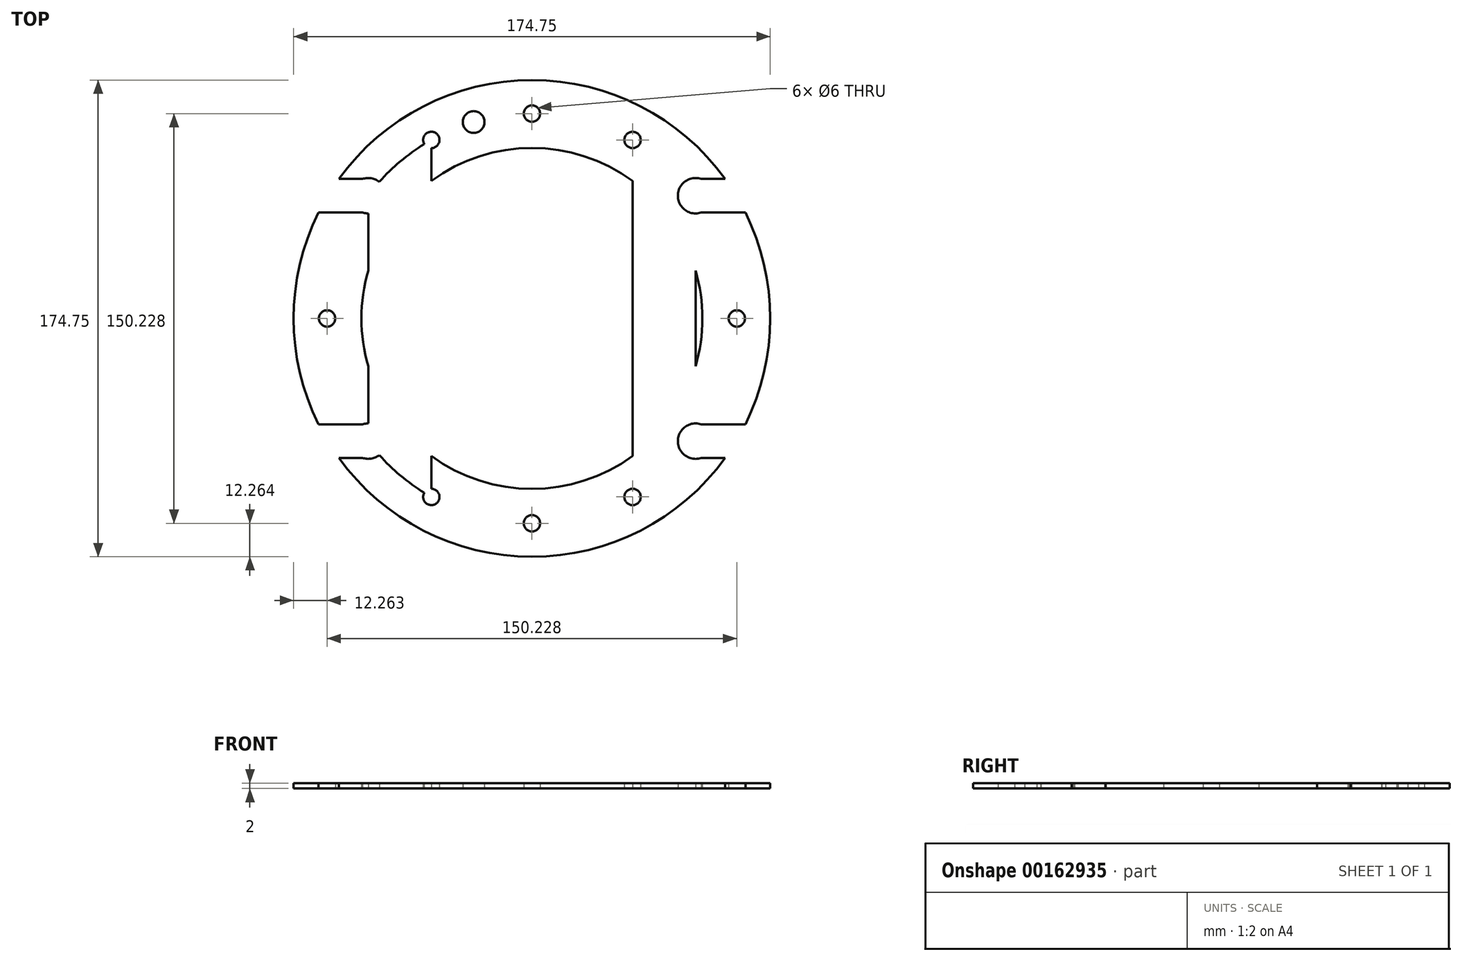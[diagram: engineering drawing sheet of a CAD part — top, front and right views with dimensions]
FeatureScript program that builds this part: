
annotation { "Feature Type Name" : "Feature", "Feature Type Description" : "" }
export const myFeature = defineFeature(function(context is Context, id is Id, definition is map)
    precondition{}
    {
        {
            var Q0;
            Q0=qCreatedBy(makeId("Top.planeOp"),FACE);
            var sketch = newSketch(context, id + "F0", { "sketchPlane" : qUnion([Q0])});
            skLineSegment(sketch, "E0.bottom", {"start": v(60.27, 43.84) * mm, "end": v(-59.73, 43.84) * mm});
            skLineSegment(sketch, "E0.top", {"start": v(60.27, -46.16) * mm, "end": v(-59.73, -46.16) * mm});
            skLineSegment(sketch, "E0.left", {"start": v(60.27, 43.84) * mm, "end": v(60.27, -46.16) * mm});
            skLineSegment(sketch, "E0.right", {"start": v(-59.73, 43.84) * mm, "end": v(-59.73, -46.16) * mm});
            skPoint(sketch, "E0.middle", {"position": v(0.27, -1.16) * mm});
            skCircle(sketch, "E1", {"center": v(60.27, 43.84) * mm, "radius": 6.5 * mm});
            skCircle(sketch, "E2", {"center": v(-59.73, 43.84) * mm, "radius": 6.5 * mm});
            skCircle(sketch, "E3", {"center": v(60.27, -46.16) * mm, "radius": 6.5 * mm});
            skCircle(sketch, "E4", {"center": v(-59.73, -46.16) * mm, "radius": 6.5 * mm});
            skCircle(sketch, "E5", {"center": v(0.27, -1.16) * mm, "radius": 87.38 * mm});
            skLineSegment(sketch, "E6.bottom", {"start": v(58.16, 49.99) * mm, "end": v(62.37, 49.99) * mm});
            skLineSegment(sketch, "E6.top", {"start": v(58.16, 37.69) * mm, "end": v(62.37, 37.69) * mm});
            skLineSegment(sketch, "E6.left", {"start": v(58.16, 49.99) * mm, "end": v(58.16, 37.69) * mm});
            skLineSegment(sketch, "E6.right", {"start": v(62.37, 49.99) * mm, "end": v(62.37, 37.69) * mm});
            skLineSegment(sketch, "E7.bottom", {"start": v(-61.84, 49.99) * mm, "end": v(-57.63, 49.99) * mm});
            skLineSegment(sketch, "E7.top", {"start": v(-61.84, 37.69) * mm, "end": v(-57.63, 37.69) * mm});
            skLineSegment(sketch, "E7.left", {"start": v(-61.84, 49.99) * mm, "end": v(-61.84, 37.69) * mm});
            skLineSegment(sketch, "E7.right", {"start": v(-57.63, 49.99) * mm, "end": v(-57.63, 37.69) * mm});
            skLineSegment(sketch, "E8.bottom", {"start": v(62.37, -40.01) * mm, "end": v(58.16, -40.01) * mm});
            skLineSegment(sketch, "E8.top", {"start": v(62.37, -52.31) * mm, "end": v(58.16, -52.31) * mm});
            skLineSegment(sketch, "E8.left", {"start": v(62.37, -40.01) * mm, "end": v(62.37, -52.31) * mm});
            skLineSegment(sketch, "E8.right", {"start": v(58.16, -40.01) * mm, "end": v(58.16, -52.31) * mm});
            skLineSegment(sketch, "E9.bottom", {"start": v(-61.84, -40.01) * mm, "end": v(-57.63, -40.01) * mm});
            skLineSegment(sketch, "E9.top", {"start": v(-61.84, -52.31) * mm, "end": v(-57.63, -52.31) * mm});
            skLineSegment(sketch, "E9.left", {"start": v(-61.84, -40.01) * mm, "end": v(-61.84, -52.31) * mm});
            skLineSegment(sketch, "E9.right", {"start": v(-57.63, -40.01) * mm, "end": v(-57.63, -52.31) * mm});
            skLineSegment(sketch, "E10.bottom", {"start": v(58.16, -40.01) * mm, "end": v(80.94, -40.01) * mm});
            skLineSegment(sketch, "E10.top", {"start": v(58.16, -52.31) * mm, "end": v(80.94, -52.31) * mm});
            skLineSegment(sketch, "E10.right", {"start": v(80.94, -40.01) * mm, "end": v(80.94, -52.31) * mm});
            skLineSegment(sketch, "E11.bottom", {"start": v(58.16, 49.99) * mm, "end": v(78.53, 49.99) * mm});
            skLineSegment(sketch, "E11.top", {"start": v(58.16, 37.69) * mm, "end": v(78.53, 37.69) * mm});
            skLineSegment(sketch, "E11.right", {"start": v(78.53, 49.99) * mm, "end": v(78.53, 37.69) * mm});
            skLineSegment(sketch, "E12.bottom", {"start": v(-57.63, 49.99) * mm, "end": v(-78, 49.99) * mm});
            skLineSegment(sketch, "E12.top", {"start": v(-57.63, 37.69) * mm, "end": v(-78, 37.69) * mm});
            skLineSegment(sketch, "E12.right", {"start": v(-78, 49.99) * mm, "end": v(-78, 37.69) * mm});
            skLineSegment(sketch, "E13.bottom", {"start": v(-57.63, -40.01) * mm, "end": v(-78, -40.01) * mm});
            skLineSegment(sketch, "E13.top", {"start": v(-57.63, -52.31) * mm, "end": v(-78, -52.31) * mm});
            skLineSegment(sketch, "E13.right", {"start": v(-78, -40.01) * mm, "end": v(-78, -52.31) * mm});
            skCircle(sketch, "E14", {"center": v(0.27, -1.16) * mm, "radius": 62.5 * mm});
            skCircle(sketch, "E15", {"center": v(0.27, 73.95) * mm, "radius": 3 * mm});
            skCircle(sketch, "E16", {"center": v(0.27, -76.28) * mm, "radius": 3 * mm});
            skCircle(sketch, "E17", {"center": v(75.38, -1.16) * mm, "radius": 3 * mm});
            skCircle(sketch, "E18", {"center": v(-74.85, -1.16) * mm, "radius": 3 * mm});
            skCircle(sketch, "E19", {"center": v(-21.11, 70.87) * mm, "radius": 4 * mm});
            skCircle(sketch, "E20", {"center": v(0.27, -1.16) * mm, "radius": 75.13 * mm});
            skLineSegment(sketch, "E21.bottom", {"start": v(37.16, 64.3) * mm, "end": v(-36.63, 64.3) * mm});
            skLineSegment(sketch, "E21.top", {"start": v(37.16, -66.61) * mm, "end": v(-36.63, -66.61) * mm});
            skLineSegment(sketch, "E21.left", {"start": v(37.16, 64.3) * mm, "end": v(37.16, -66.61) * mm});
            skLineSegment(sketch, "E21.right", {"start": v(-36.63, 64.3) * mm, "end": v(-36.63, -66.61) * mm});
            skCircle(sketch, "E22", {"center": v(-36.63, 64.3) * mm, "radius": 3 * mm});
            skCircle(sketch, "E23", {"center": v(37.16, 64.3) * mm, "radius": 3 * mm});
            skCircle(sketch, "E24", {"center": v(37.16, -66.61) * mm, "radius": 3 * mm});
            skCircle(sketch, "E25", {"center": v(-36.63, -66.61) * mm, "radius": 3 * mm});
            skSolve(sketch);
        }
        {
            var Q0;
            {var subQ0=sQuery(id+"F0.wireOp",EDGE,"E11.bottom");var subQ3=sQuery(id+"F0.wireOp",EDGE,"E5");var subQ4=makeQuery(id+"F0.imprint","INTERSECT",VERTEX,{"derivedFrom":[subQ3,subQ0]});Q0=makeQuery(id+"F0.imprint","IMPRINT",FACE,{"disambiguationData":[TD([[makeQuery(id+"F0.imprint","IMPRINT",EDGE,{"disambiguationData":[TD([[subQ4,-1.0]])],"derivedFrom":subQ3}),1.0]])]});}
            var Q1;
            {var subQ0=sQuery(id+"F0.wireOp",EDGE,"E20");var subQ1=sQuery(id+"F0.wireOp",EDGE,"E15");var subQ5=makeQuery(id+"F0.imprint","INTERSECT",VERTEX,{"disambiguationData":[OD(0.0)],"derivedFrom":[subQ1,subQ0]});Q1=makeQuery(id+"F0.imprint","IMPRINT",FACE,{"disambiguationData":[TD([[makeQuery(id+"F0.imprint","IMPRINT",EDGE,{"disambiguationData":[TD([[subQ5,1.0]])],"derivedFrom":subQ1}),-1.0]])]});}
            var Q2;
            {var subQ0=sQuery(id+"F0.wireOp",EDGE,"E21.left");var subQ1=sQuery(id+"F0.wireOp",EDGE,"E14");var subQ2=makeQuery(id+"F0.imprint","INTERSECT",VERTEX,{"disambiguationData":[OD(0.0)],"derivedFrom":[subQ1,subQ0]});Q2=makeQuery(id+"F0.imprint","IMPRINT",FACE,{"disambiguationData":[TD([[makeQuery(id+"F0.imprint","IMPRINT",EDGE,{"disambiguationData":[TD([[subQ2,-1.0]])],"derivedFrom":subQ1}),-1.0]])]});}
            var Q3;
            {var subQ0=sQuery(id+"F0.wireOp",EDGE,"E14");var subQ1=sQuery(id+"F0.wireOp",EDGE,"E0.bottom");var subQ2=makeQuery(id+"F0.imprint","INTERSECT",VERTEX,{"disambiguationData":[OD(1.0)],"derivedFrom":[subQ1,subQ0]});Q3=makeQuery(id+"F0.imprint","IMPRINT",FACE,{"disambiguationData":[TD([[makeQuery(id+"F0.imprint","IMPRINT",EDGE,{"disambiguationData":[TD([[subQ2,-1.0]])],"derivedFrom":subQ1}),-1.0]])]});}
            var Q4;
            {var subQ2=sQuery(id+"F0.wireOp",EDGE,"E0.bottom");var subQ6=sQuery(id+"F0.wireOp",EDGE,"E14");var subQ8=makeQuery(id+"F0.imprint","INTERSECT",VERTEX,{"disambiguationData":[OD(1.0)],"derivedFrom":[subQ2,subQ6]});Q4=makeQuery(id+"F0.imprint","IMPRINT",FACE,{"disambiguationData":[TD([[makeQuery(id+"F0.imprint","IMPRINT",EDGE,{"disambiguationData":[TD([[subQ8,-1.0]])],"derivedFrom":subQ2}),1.0]])]});}
            var Q5;
            {var subQ3=sQuery(id+"F0.wireOp",EDGE,"E0.right");var subQ5=sQuery(id+"F0.wireOp",EDGE,"E2");var subQ6=makeQuery(id+"F0.imprint","INTERSECT",VERTEX,{"derivedFrom":[subQ3,subQ5]});Q5=makeQuery(id+"F0.imprint","IMPRINT",FACE,{"disambiguationData":[TD([[makeQuery(id+"F0.imprint","IMPRINT",EDGE,{"disambiguationData":[TD([[subQ6,-1.0]])],"derivedFrom":subQ3}),-1.0]])]});}
            var Q6;
            {var subQ0=sQuery(id+"F0.wireOp",EDGE,"E13.right");var subQ1=sQuery(id+"F0.wireOp",EDGE,"E13.bottom");var subQ2=makeQuery(id+"F0.imprint","INTERSECT",VERTEX,{"derivedFrom":[subQ1,subQ0]});Q6=makeQuery(id+"F0.imprint","IMPRINT",FACE,{"disambiguationData":[TD([[makeQuery(id+"F0.imprint","IMPRINT",EDGE,{"disambiguationData":[TD([[subQ2,1.0]])],"derivedFrom":subQ1}),-1.0]])]});}
            var Q7;
            {var subQ1=sQuery(id+"F0.wireOp",EDGE,"E1");var subQ6=sQuery(id+"F0.wireOp",EDGE,"E0.bottom");var subQ10=makeQuery(id+"F0.imprint","INTERSECT",VERTEX,{"derivedFrom":[subQ6,subQ1]});Q7=makeQuery(id+"F0.imprint","IMPRINT",FACE,{"disambiguationData":[TD([[makeQuery(id+"F0.imprint","IMPRINT",EDGE,{"disambiguationData":[TD([[subQ10,-1.0]])],"derivedFrom":subQ6}),-1.0]])]});}
            var Q8;
            {var subQ0=sQuery(id+"F0.wireOp",EDGE,"E1");var subQ4=sQuery(id+"F0.wireOp",EDGE,"E0.bottom");var subQ5=makeQuery(id+"F0.imprint","INTERSECT",VERTEX,{"derivedFrom":[subQ4,subQ0]});Q8=makeQuery(id+"F0.imprint","IMPRINT",FACE,{"disambiguationData":[TD([[makeQuery(id+"F0.imprint","IMPRINT",EDGE,{"disambiguationData":[TD([[subQ5,-1.0]])],"derivedFrom":subQ4}),1.0]])]});}
            var Q9;
            {var subQ3=sQuery(id+"F0.wireOp",EDGE,"E0.left");var subQ6=sQuery(id+"F0.wireOp",EDGE,"E1");var subQ8=makeQuery(id+"F0.imprint","INTERSECT",VERTEX,{"derivedFrom":[subQ3,subQ6]});Q9=makeQuery(id+"F0.imprint","IMPRINT",FACE,{"disambiguationData":[TD([[makeQuery(id+"F0.imprint","IMPRINT",EDGE,{"disambiguationData":[TD([[subQ8,-1.0]])],"derivedFrom":subQ3}),1.0]])]});}
            var Q10;
            {var subQ5=sQuery(id+"F0.wireOp",EDGE,"E5");var subQ8=sQuery(id+"F0.wireOp",EDGE,"E10.bottom");var subQ9=makeQuery(id+"F0.imprint","INTERSECT",VERTEX,{"derivedFrom":[subQ5,subQ8]});Q10=makeQuery(id+"F0.imprint","IMPRINT",FACE,{"disambiguationData":[TD([[makeQuery(id+"F0.imprint","IMPRINT",EDGE,{"disambiguationData":[TD([[subQ9,1.0]])],"derivedFrom":subQ8}),1.0]])]});}
            var Q11;
            {var subQ0=sQuery(id+"F0.wireOp",EDGE,"E3");var subQ2=sQuery(id+"F0.wireOp",EDGE,"E0.top");var subQ3=makeQuery(id+"F0.imprint","INTERSECT",VERTEX,{"derivedFrom":[subQ2,subQ0]});Q11=makeQuery(id+"F0.imprint","IMPRINT",FACE,{"disambiguationData":[TD([[makeQuery(id+"F0.imprint","IMPRINT",EDGE,{"disambiguationData":[TD([[subQ3,-1.0]])],"derivedFrom":subQ2}),-1.0]])]});}
            var Q12;
            {var subQ1=sQuery(id+"F0.wireOp",EDGE,"E3");var subQ6=sQuery(id+"F0.wireOp",EDGE,"E0.top");var subQ10=makeQuery(id+"F0.imprint","INTERSECT",VERTEX,{"derivedFrom":[subQ6,subQ1]});Q12=makeQuery(id+"F0.imprint","IMPRINT",FACE,{"disambiguationData":[TD([[makeQuery(id+"F0.imprint","IMPRINT",EDGE,{"disambiguationData":[TD([[subQ10,-1.0]])],"derivedFrom":subQ6}),1.0]])]});}
            var Q13;
            {var subQ13=sQuery(id+"F0.wireOp",EDGE,"E13.top");var subQ15=sQuery(id+"F0.wireOp",EDGE,"E5");var subQ16=makeQuery(id+"F0.imprint","INTERSECT",VERTEX,{"derivedFrom":[subQ15,subQ13]});Q13=makeQuery(id+"F0.imprint","IMPRINT",FACE,{"disambiguationData":[TD([[makeQuery(id+"F0.imprint","IMPRINT",EDGE,{"disambiguationData":[TD([[subQ16,-1.0]])],"derivedFrom":subQ15}),1.0]])]});}
            var Q14;
            {var subQ1=sQuery(id+"F0.wireOp",EDGE,"E14");var subQ5=sQuery(id+"F0.wireOp",EDGE,"E21.right");var subQ6=makeQuery(id+"F0.imprint","INTERSECT",VERTEX,{"disambiguationData":[OD(1.0)],"derivedFrom":[subQ1,subQ5]});Q14=makeQuery(id+"F0.imprint","IMPRINT",FACE,{"disambiguationData":[TD([[makeQuery(id+"F0.imprint","IMPRINT",EDGE,{"disambiguationData":[TD([[subQ6,-1.0]])],"derivedFrom":subQ1}),-1.0]])]});}
            var Q15;
            {var subQ5=sQuery(id+"F0.wireOp",EDGE,"E20");var subQ7=sQuery(id+"F0.wireOp",EDGE,"E16");var subQ10=makeQuery(id+"F0.imprint","INTERSECT",VERTEX,{"disambiguationData":[OD(0.0)],"derivedFrom":[subQ7,subQ5]});Q15=makeQuery(id+"F0.imprint","IMPRINT",FACE,{"disambiguationData":[TD([[makeQuery(id+"F0.imprint","IMPRINT",EDGE,{"disambiguationData":[TD([[subQ10,1.0]])],"derivedFrom":subQ7}),-1.0]])]});}
            var Q16;
            {var subQ0=sQuery(id+"F0.wireOp",EDGE,"E14");var subQ1=sQuery(id+"F0.wireOp",EDGE,"E0.top");var subQ2=makeQuery(id+"F0.imprint","INTERSECT",VERTEX,{"disambiguationData":[OD(1.0)],"derivedFrom":[subQ1,subQ0]});Q16=makeQuery(id+"F0.imprint","IMPRINT",FACE,{"disambiguationData":[TD([[makeQuery(id+"F0.imprint","IMPRINT",EDGE,{"disambiguationData":[TD([[subQ2,-1.0]])],"derivedFrom":subQ1}),1.0]])]});}
            var Q17;
            {var subQ2=sQuery(id+"F0.wireOp",EDGE,"E0.top");var subQ6=sQuery(id+"F0.wireOp",EDGE,"E14");var subQ8=makeQuery(id+"F0.imprint","INTERSECT",VERTEX,{"disambiguationData":[OD(1.0)],"derivedFrom":[subQ2,subQ6]});Q17=makeQuery(id+"F0.imprint","IMPRINT",FACE,{"disambiguationData":[TD([[makeQuery(id+"F0.imprint","IMPRINT",EDGE,{"disambiguationData":[TD([[subQ8,-1.0]])],"derivedFrom":subQ2}),-1.0]])]});}
            extrude(context, id + "F1", {"entities" : qUnion([Q0, Q1, Q2, Q3, Q4, Q5, Q6, Q7, Q8, Q9, Q10, Q11, Q12, Q13, Q14, Q15, Q16, Q17]), "depth" : 2 * mm});
        }
    });
